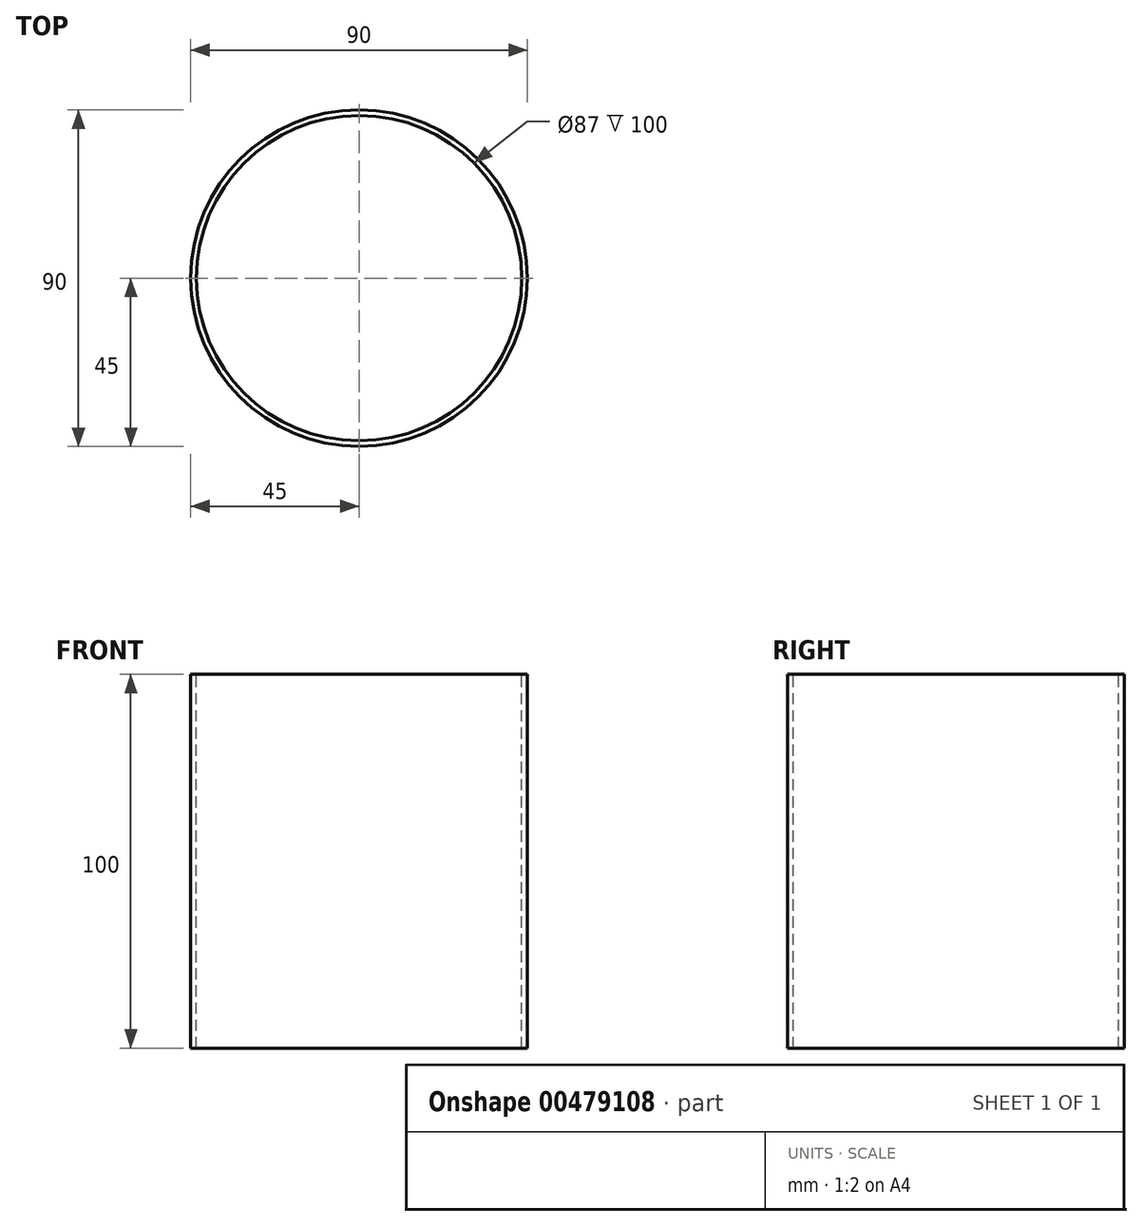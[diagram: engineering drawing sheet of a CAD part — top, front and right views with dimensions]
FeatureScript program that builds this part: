
annotation { "Feature Type Name" : "Feature", "Feature Type Description" : "" }
export const myFeature = defineFeature(function(context is Context, id is Id, definition is map)
    precondition{}
    {
        {
            var Q0;
            Q0=qCreatedBy(makeId("Top.planeOp"),FACE);
            var sketch = newSketch(context, id + "F0", { "sketchPlane" : qUnion([Q0])});
            skCircle(sketch, "E0", {"center": v(0, 0) * mm, "radius": 45 * mm});
            skSolve(sketch);
        }
        {
            var Q0;
            Q0=makeQuery(id+"F0.imprint","IMPRINT",FACE,{"disambiguationData":[TD([[makeQuery(id+"F0.imprint","IMPRINT",EDGE,{"derivedFrom":sQuery(id+"F0.wireOp",EDGE,"E0")}),1.0]])]});
            extrude(context, id + "F1", {"entities" : qUnion([Q0]), "depth" : 100 * mm, "offsetDistance" : 25 * mm});
        }
        {
            var Q0;
            Q0=makeQuery(id+"F1.opExtrude","CAP_FACE",FACE,{"disambiguationData":[OSD([sQuery(id+"F0.wireOp",EDGE,"E0")])],"isStart":false});
            var sketch = newSketch(context, id + "F2", { "sketchPlane" : qUnion([Q0])});
            skCircle(sketch, "E1", {"center": v(0, 0) * mm, "radius": 43.5 * mm});
            skSolve(sketch);
        }
        {
            var Q0;
            Q0=qSketchRegion(id+"F2",true);
            var Q1;
            Q1 = qSketchRegion(id + "F0", true);
            extrude(context, id + "F3", {"entities" : qUnion([Q0, Q1]), "operationType" : NewBodyOperationType.REMOVE, "oppositeDirection" : true, "depth" : 4000 * mm, "offsetDistance" : 25 * mm});
        }
    });
